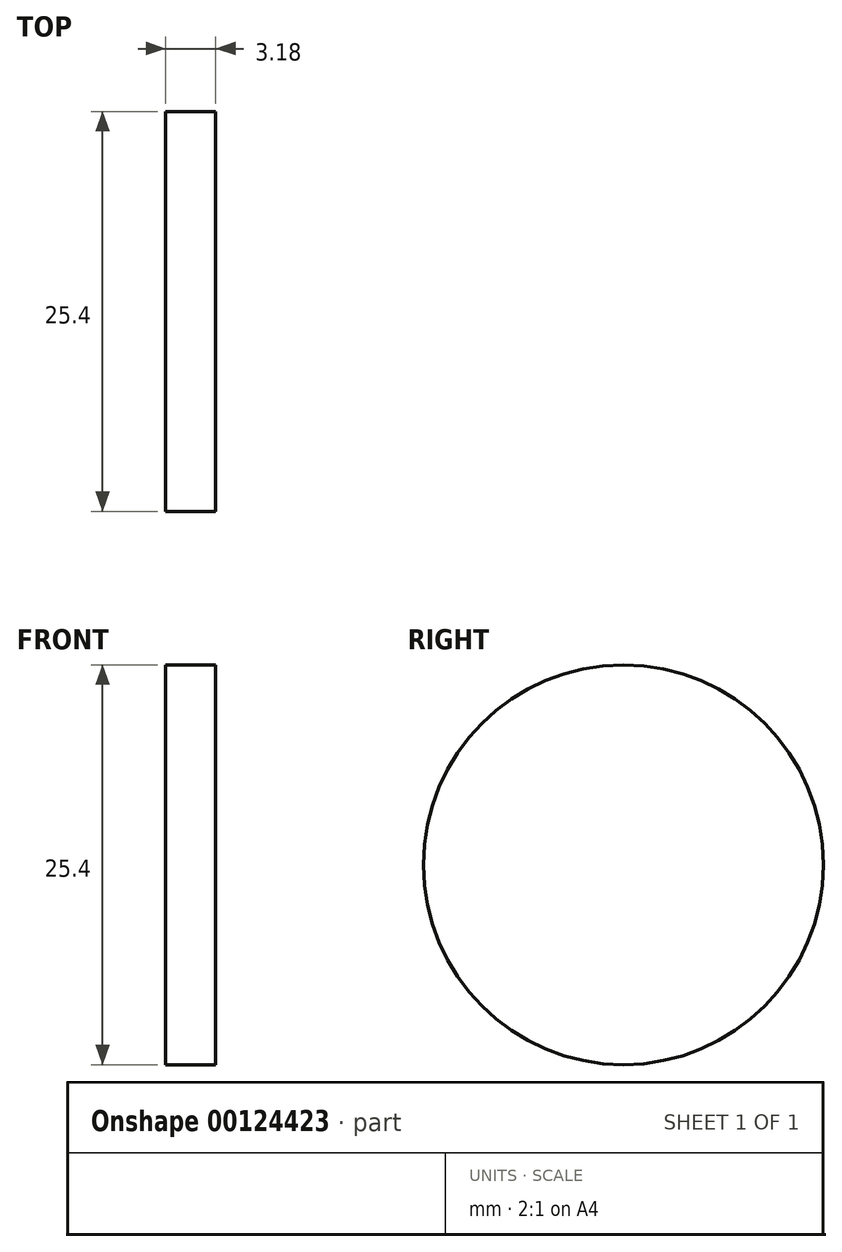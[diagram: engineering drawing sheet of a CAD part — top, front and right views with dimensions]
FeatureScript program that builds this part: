
annotation { "Feature Type Name" : "Feature", "Feature Type Description" : "" }
export const myFeature = defineFeature(function(context is Context, id is Id, definition is map)
    precondition{}
    {
        {
            var Q0;
            Q0=qCreatedBy(makeId("Right.planeOp"),FACE);
            var sketch = newSketch(context, id + "F0", { "sketchPlane" : qUnion([Q0])});
            skCircle(sketch, "E0", {"center": v(0, 0) * mm, "radius": 12.7 * mm});
            skSolve(sketch);
        }
        {
            var Q0;
            Q0=makeQuery(id+"F0.imprint","IMPRINT",FACE,{"disambiguationData":[TD([[makeQuery(id+"F0.imprint","IMPRINT",EDGE,{"derivedFrom":sQuery(id+"F0.wireOp",EDGE,"E0")}),1.0]])]});
            extrude(context, id + "F1", {"entities" : qUnion([Q0]), "depth" : 3.17 * mm});
        }
    });
